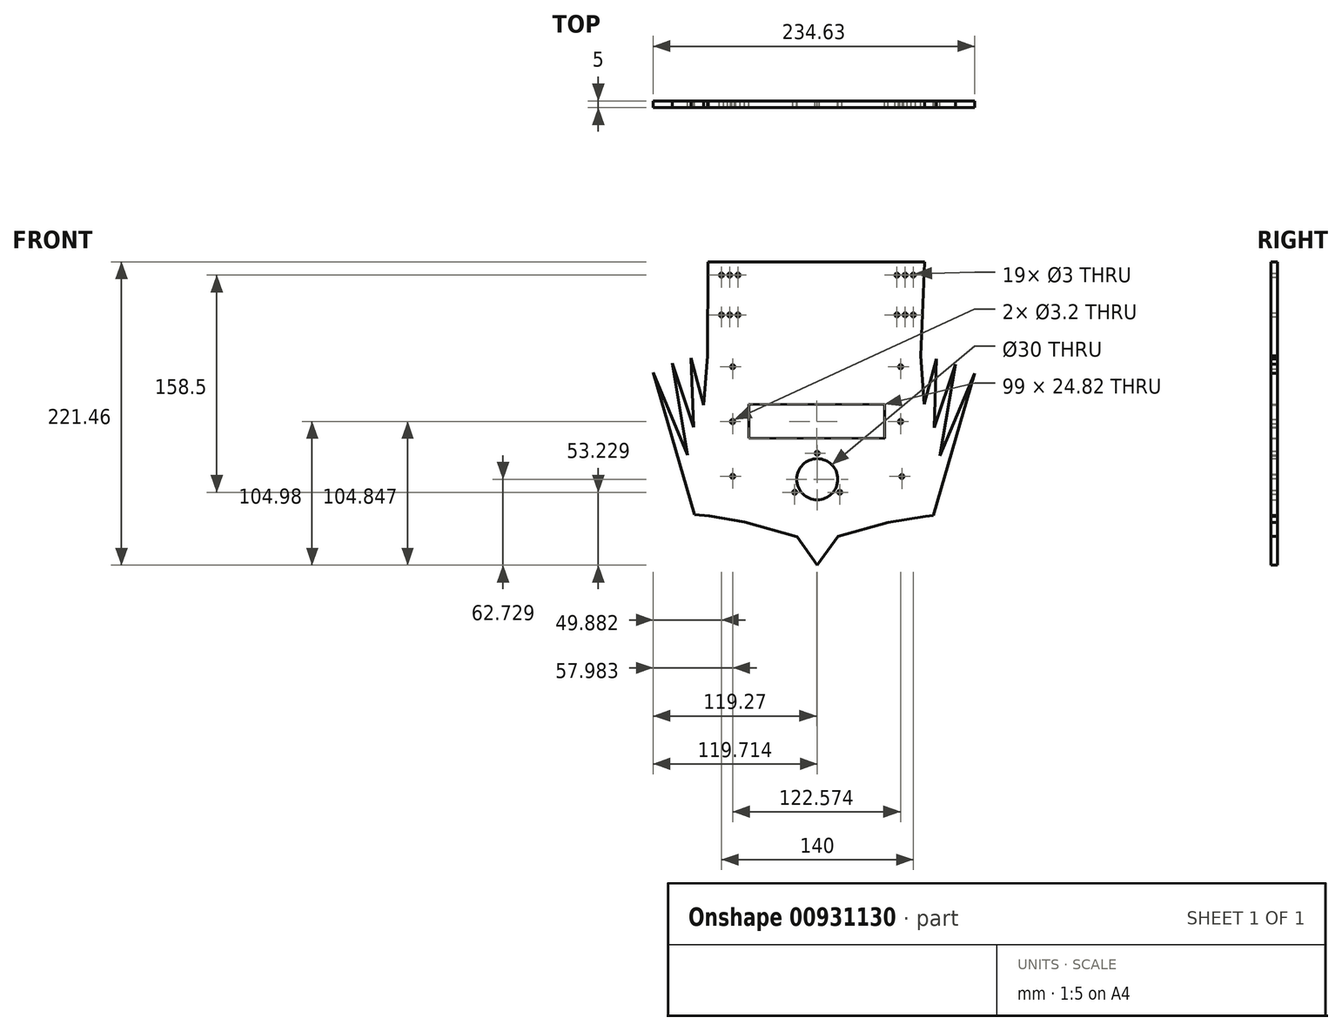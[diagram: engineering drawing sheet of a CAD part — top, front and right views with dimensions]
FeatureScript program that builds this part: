
annotation { "Feature Type Name" : "Feature", "Feature Type Description" : "" }
export const myFeature = defineFeature(function(context is Context, id is Id, definition is map)
    precondition{}
    {
        {
            var Q0;
            Q0=qCreatedBy(makeId("Front.planeOp"),FACE);
            var sketch = newSketch(context, id + "F0", { "sketchPlane" : qUnion([Q0])});
            skCircle(sketch, "E0", {"center": v(-84.94, 71.09) * mm, "radius": 1.5 * mm});
            skCircle(sketch, "E1.0.1.0", {"center": v(-84.94, 100.09) * mm, "radius": 1.5 * mm});
            skCircle(sketch, "E1.1.0.0", {"center": v(-78.94, 71.09) * mm, "radius": 1.5 * mm});
            skCircle(sketch, "E1.1.1.0", {"center": v(-78.94, 100.09) * mm, "radius": 1.5 * mm});
            skCircle(sketch, "E1.2.0.0", {"center": v(-72.94, 71.09) * mm, "radius": 1.5 * mm});
            skCircle(sketch, "E1.2.1.0", {"center": v(-72.94, 100.09) * mm, "radius": 1.5 * mm});
            skLineSegment(sketch, "E1.direction1", {"start": v(-84.94, 71.09) * mm, "end": v(-78.94, 71.09) * mm, "construction": true});
            skLineSegment(sketch, "E1.direction2", {"start": v(-84.94, 71.09) * mm, "end": v(-84.94, 100.09) * mm, "construction": true});
            skLineSegment(sketch, "E2", {"start": v(-14.94, 73.97) * mm, "end": v(-14.94, 101.77) * mm});
            skCircle(sketch, "E3.MirrorC", {"center": v(55.06, 100.09) * mm, "radius": 1.5 * mm});
            skLineSegment(sketch, "E4.MirrorCS", {"start": v(55.06, 71.09) * mm, "end": v(49.06, 71.09) * mm, "construction": true});
            skCircle(sketch, "E5.MirrorC", {"center": v(43.06, 71.09) * mm, "radius": 1.5 * mm});
            skCircle(sketch, "E6.MirrorC", {"center": v(55.06, 71.09) * mm, "radius": 1.5 * mm});
            skCircle(sketch, "E7.MirrorC", {"center": v(49.06, 71.09) * mm, "radius": 1.5 * mm});
            skCircle(sketch, "E8.MirrorC", {"center": v(49.06, 100.09) * mm, "radius": 1.5 * mm});
            skCircle(sketch, "E9.MirrorC", {"center": v(43.06, 100.09) * mm, "radius": 1.5 * mm});
            skLineSegment(sketch, "E10.MirrorCS", {"start": v(55.06, 71.09) * mm, "end": v(55.06, 100.09) * mm, "construction": true});
            skLineSegment(sketch, "E11.bottom", {"start": v(-94.95, 109.82) * mm, "end": v(63.26, 109.65) * mm});
            skLineSegment(sketch, "E11.left", {"start": v(-94.95, 109.82) * mm, "end": v(-95.44, -71.9) * mm});
            skPoint(sketch, "E12", {"position": v(714775.97, -668.2) * mm});
            skCircle(sketch, "E13", {"center": v(-15.1, -48.91) * mm, "radius": 15 * mm});
            skLineSegment(sketch, "E14", {"start": v(-80.84, -6.8) * mm, "end": v(-65.05, 5.75) * mm});
            skLineSegment(sketch, "E15", {"start": v(-65.05, 5.75) * mm, "end": v(33.95, 5.49) * mm});
            skLineSegment(sketch, "E16", {"start": v(33.95, 5.49) * mm, "end": v(49.74, -6.8) * mm});
            skLineSegment(sketch, "E17", {"start": v(49.74, -6.8) * mm, "end": v(33.95, -19.07) * mm});
            skLineSegment(sketch, "E18", {"start": v(33.95, -19.07) * mm, "end": v(-65.05, -18.8) * mm});
            skLineSegment(sketch, "E19", {"start": v(-65.05, -18.8) * mm, "end": v(-80.84, -6.8) * mm});
            skLineSegment(sketch, "E20", {"start": v(-65.05, 5.75) * mm, "end": v(-65.05, -18.8) * mm});
            skLineSegment(sketch, "E21", {"start": v(33.95, 5.49) * mm, "end": v(33.95, -19.07) * mm});
            skCircle(sketch, "E22", {"center": v(-76.84, -6.8) * mm, "radius": 1.6 * mm});
            skCircle(sketch, "E23", {"center": v(45.74, -6.8) * mm, "radius": 1.6 * mm});
            skLineSegment(sketch, "E24", {"start": v(-15.1, -48.91) * mm, "end": v(30.86, -48.91) * mm});
            skPoint(sketch, "E25.start.orphan", {"position": v(-95.13, 41.09) * mm});
            skPoint(sketch, "E26.start.orphan", {"position": v(60.27, 41.09) * mm});
            skLineSegment(sketch, "E27", {"start": v(-95.13, 41.09) * mm, "end": v(-104.8, -74.78) * mm});
            skLineSegment(sketch, "E28", {"start": v(-104.8, -74.78) * mm, "end": v(-15.1, -82.26) * mm});
            skLineSegment(sketch, "E29", {"start": v(-15.1, -82.26) * mm, "end": v(69.62, -75.45) * mm});
            skLineSegment(sketch, "E30", {"start": v(-15.1, -89.09) * mm, "end": v(-93.98, -75.69) * mm});
            skLineSegment(sketch, "E31", {"start": v(-68.06, -80.09) * mm, "end": v(-15.1, -94.94) * mm});
            skLineSegment(sketch, "E32", {"start": v(-15.1, -94.94) * mm, "end": v(37.86, -80.14) * mm});
            skLineSegment(sketch, "E33", {"start": v(-104.8, -74.78) * mm, "end": v(-134.82, 29.02) * mm});
            skLineSegment(sketch, "E34", {"start": v(-134.82, 29.02) * mm, "end": v(-109.63, -31.2) * mm});
            skLineSegment(sketch, "E35", {"start": v(-109.63, -31.2) * mm, "end": v(-120.81, 35.77) * mm});
            skLineSegment(sketch, "E36", {"start": v(-107.28, 39.75) * mm, "end": v(-98.11, 5.39) * mm});
            skLineSegment(sketch, "E37.MirrorCS", {"start": v(-14.99, -89.15) * mm, "end": v(63.8, -75.92) * mm});
            skPoint(sketch, "E38.orphan", {"position": v(-15.1, 126.09) * mm});
            skLineSegment(sketch, "E39", {"start": v(45.74, -6.8) * mm, "end": v(45.74, -5.2) * mm});
            skCircle(sketch, "E40", {"center": v(45.74, 33.2) * mm, "radius": 1.5 * mm});
            skCircle(sketch, "E41", {"center": v(-76.84, -46.8) * mm, "radius": 1.5 * mm});
            skCircle(sketch, "E42", {"center": v(-76.84, 33.2) * mm, "radius": 1.5 * mm});
            skCircle(sketch, "E43.MirrorC", {"center": v(46.67, -46.9) * mm, "radius": 1.5 * mm});
            skLineSegment(sketch, "E44.MirrorCS", {"start": v(60.27, 41.09) * mm, "end": v(69.62, -75.45) * mm});
            skLineSegment(sketch, "E45.MirrorCS", {"start": v(63.26, 109.65) * mm, "end": v(55.34, -72.04) * mm});
            skLineSegment(sketch, "E46.MirrorCS", {"start": v(99.81, 28.4) * mm, "end": v(74.5, -31.78) * mm});
            skLineSegment(sketch, "E47.MirrorCS", {"start": v(74.5, -31.78) * mm, "end": v(85.81, 35.16) * mm});
            skLineSegment(sketch, "E48.MirrorCS", {"start": v(71.86, 39.06) * mm, "end": v(63.09, 5.97) * mm});
            skLineSegment(sketch, "E49.MirrorCS", {"start": v(69.62, -75.45) * mm, "end": v(99.81, 28.4) * mm});
            skLineSegment(sketch, "E50.MirrorCS", {"start": v(55.34, -72.04) * mm, "end": v(-95.44, -71.9) * mm});
            skLineSegment(sketch, "E51.MirrorCS", {"start": v(63.8, -75.92) * mm, "end": v(-15.1, -82.26) * mm});
            skPoint(sketch, "E52.trimOffspring.end.orphan", {"position": v(-14.94, 109.73) * mm});
            skLineSegment(sketch, "E53", {"start": v(-120.81, 35.77) * mm, "end": v(-105.16, -11) * mm});
            skLineSegment(sketch, "E54", {"start": v(-105.16, -11) * mm, "end": v(-107.25, 39.69) * mm});
            skLineSegment(sketch, "E55", {"start": v(85.81, 35.16) * mm, "end": v(70.21, -11.23) * mm});
            skLineSegment(sketch, "E56", {"start": v(70.21, -11.23) * mm, "end": v(71.86, 39.06) * mm});
            skLineSegment(sketch, "E57", {"start": v(0, -90.72) * mm, "end": v(-15.1, -111.64) * mm});
            skLineSegment(sketch, "E58", {"start": v(-15.1, -111.64) * mm, "end": v(-29.63, -90.87) * mm});
            skCircle(sketch, "E59", {"center": v(-15.1, -48.91) * mm, "radius": 19 * mm, "construction": true});
            skCircle(sketch, "E60", {"center": v(-15.1, -29.91) * mm, "radius": 1.5 * mm});
            skCircle(sketch, "E61.1.0", {"center": v(-31.56, -58.41) * mm, "radius": 1.5 * mm});
            skCircle(sketch, "E61.2.0", {"center": v(1.35, -58.41) * mm, "radius": 1.5 * mm});
            skSolve(sketch);
        }
        {
            var Q0;
            Q0=makeQuery(id+"F0.imprint","IMPRINT",FACE,{"disambiguationData":[TD([[makeQuery(id+"F0.imprint","IMPRINT",EDGE,{"derivedFrom":sQuery(id+"F0.wireOp",EDGE,"E0")}),-1.0]])]});
            var Q1;
            {var subQ11=sQuery(id+"F0.wireOp",EDGE,"E50.MirrorCS");Q1=makeQuery(id+"F0.imprint","IMPRINT",FACE,{"disambiguationData":[TD([[makeQuery(id+"F0.imprint","IMPRINT",EDGE,{"derivedFrom":subQ11}),1.0]])]});}
            var Q2;
            {var subQ0=sQuery(id+"F0.wireOp",EDGE,"E33");Q2=makeQuery(id+"F0.imprint","IMPRINT",FACE,{"disambiguationData":[TD([[makeQuery(id+"F0.imprint","IMPRINT",EDGE,{"derivedFrom":subQ0}),-1.0]])]});}
            var Q3;
            Q3=makeQuery(id+"F0.imprint","IMPRINT",FACE,{"disambiguationData":[TD([[makeQuery(id+"F0.imprint","IMPRINT",EDGE,{"derivedFrom":sQuery(id+"F0.wireOp",EDGE,"E14")}),-1.0]])]});
            var Q4;
            Q4=makeQuery(id+"F0.imprint","IMPRINT",FACE,{"disambiguationData":[TD([[makeQuery(id+"F0.imprint","IMPRINT",EDGE,{"derivedFrom":sQuery(id+"F0.wireOp",EDGE,"E46.MirrorCS")}),1.0]])]});
            var Q5;
            Q5=makeQuery(id+"F0.imprint","IMPRINT",FACE,{"disambiguationData":[TD([[makeQuery(id+"F0.imprint","IMPRINT",EDGE,{"derivedFrom":sQuery(id+"F0.wireOp",EDGE,"E16")}),-1.0]])]});
            var Q6;
            {var subQ0=sQuery(id+"F0.wireOp",EDGE,"E31");Q6=makeQuery(id+"F0.imprint","IMPRINT",FACE,{"disambiguationData":[TD([[makeQuery(id+"F0.imprint","IMPRINT",EDGE,{"derivedFrom":subQ0}),1.0]])]});}
            extrude(context, id + "F1", {"entities" : qUnion([Q0, Q1, Q2, Q3, Q4, Q5, Q6]), "depth" : 5 * mm, "offsetDistance" : 25 * mm});
        }
        {
            var Q0;
            {var subQ4=sQuery(id+"F0.wireOp",EDGE,"E57");Q0=makeQuery(id+"F0.imprint","IMPRINT",FACE,{"disambiguationData":[TD([[makeQuery(id+"F0.imprint","IMPRINT",EDGE,{"derivedFrom":subQ4}),-1.0]])]});}
            extrude(context, id + "F2", {"entities" : qUnion([Q0]), "operationType" : NewBodyOperationType.ADD, "depth" : 5 * mm, "offsetDistance" : 25 * mm});
        }
    });
